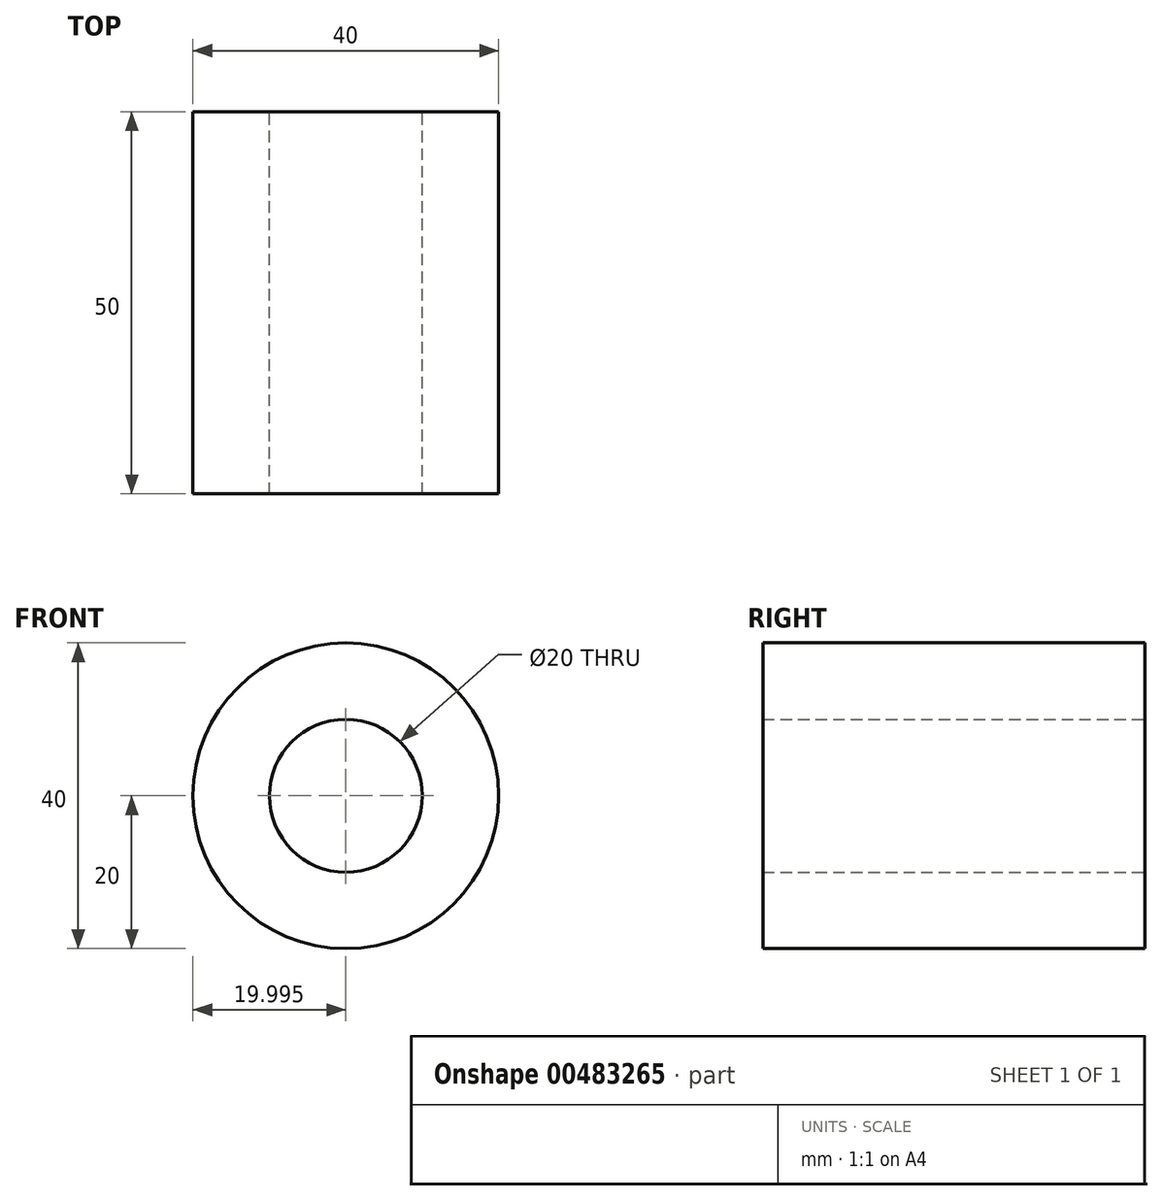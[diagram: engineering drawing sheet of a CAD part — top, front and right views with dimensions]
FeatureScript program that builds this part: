
annotation { "Feature Type Name" : "Feature", "Feature Type Description" : "" }
export const myFeature = defineFeature(function(context is Context, id is Id, definition is map)
    precondition{}
    {
        {
            var Q0;
            Q0=qCreatedBy(makeId("Front.planeOp"),FACE);
            var sketch = newSketch(context, id + "F0", { "sketchPlane" : qUnion([Q0])});
            skCircle(sketch, "E0", {"center": v(-45.1, 0) * mm, "radius": 10 * mm});
            skCircle(sketch, "E1", {"center": v(-45.1, 0) * mm, "radius": 20 * mm});
            skCircle(sketch, "E2", {"center": v(52.88, 24.66) * mm, "radius": 10 * mm});
            skCircle(sketch, "E3", {"center": v(52.88, 24.66) * mm, "radius": 20 * mm});
            skLineSegment(sketch, "E4", {"start": v(72.88, 21.56) * mm, "end": v(72.88, -10.44) * mm});
            skLineSegment(sketch, "E5", {"start": v(52.88, 24.66) * mm, "end": v(0, 24.66) * mm});
            skCircle(sketch, "E6", {"center": v(0, 24.66) * mm, "radius": 27.29 * mm});
            skLineSegment(sketch, "E7.bottom", {"start": v(82.58, 43.74) * mm, "end": v(-82.58, 43.74) * mm});
            skLineSegment(sketch, "E7.top", {"start": v(82.58, -43.74) * mm, "end": v(-82.58, -43.74) * mm});
            skLineSegment(sketch, "E7.left", {"start": v(82.58, 43.74) * mm, "end": v(82.58, -43.74) * mm});
            skLineSegment(sketch, "E7.right", {"start": v(-82.58, 43.74) * mm, "end": v(-82.58, -43.74) * mm});
            skPoint(sketch, "E7.middle", {"position": v(0, 0) * mm});
            skSolve(sketch);
        }
        {
            var Q0;
            Q0=makeQuery(id+"F0.imprint","IMPRINT",FACE,{"disambiguationData":[TD([[makeQuery(id+"F0.imprint","IMPRINT",EDGE,{"derivedFrom":sQuery(id+"F0.wireOp",EDGE,"E0")}),-1.0]])]});
            extrude(context, id + "F1", {"entities" : qUnion([Q0]), "depth" : 50 * mm});
        }
    });
